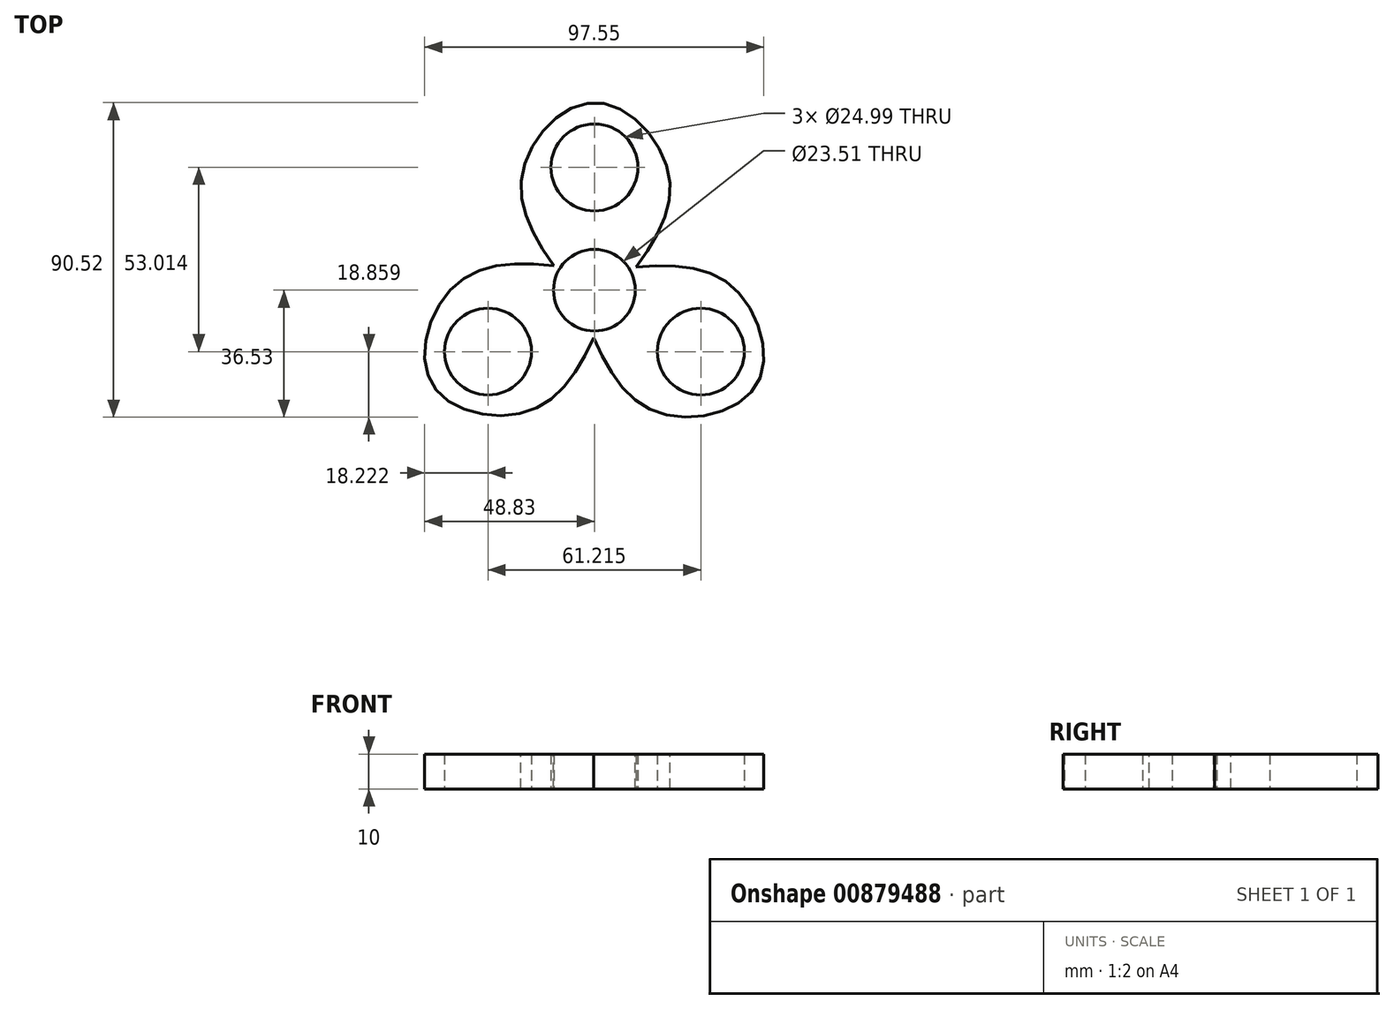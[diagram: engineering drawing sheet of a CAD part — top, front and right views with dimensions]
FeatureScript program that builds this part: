
annotation { "Feature Type Name" : "Feature", "Feature Type Description" : "" }
export const myFeature = defineFeature(function(context is Context, id is Id, definition is map)
    precondition{}
    {
        {
            var Q0;
            Q0=qCreatedBy(makeId("Top.planeOp"),FACE);
            var sketch = newSketch(context, id + "F0", { "sketchPlane" : qUnion([Q0])});
            skFitSpline(sketch, "E0", {"points": [v(-6.47, 0) * mm, v(-20.9, 32.64) * mm, v(0, 54) * mm, v(21.5, 32.64) * mm, v(7.07, 0) * mm], "startDerivative": vector(-92.56, 122.62) * mm, "endDerivative": vector(-93.29, -122.7) * mm});
            skLineSegment(sketch, "E1", {"start": v(-6.47, 0) * mm, "end": v(7.07, 0) * mm});
            skSolve(sketch);
        }
        {
            var Q0;
            Q0=makeQuery(id+"F0.imprint","IMPRINT",FACE,{"disambiguationData":[TD([[makeQuery(id+"F0.imprint","IMPRINT",EDGE,{"derivedFrom":sQuery(id+"F0.wireOp",EDGE,"E0")}),-1.0]])]});
            var sketch = newSketch(context, id + "F1", { "sketchPlane" : qUnion([Q0])});
            skCircle(sketch, "E2", {"center": v(0, 35.34) * mm, "radius": 12.5 * mm});
            skSolve(sketch);
        }
        {
            var Q0;
            Q0=makeQuery(id+"F0.imprint","IMPRINT",FACE,{"disambiguationData":[TD([[makeQuery(id+"F0.imprint","IMPRINT",EDGE,{"derivedFrom":sQuery(id+"F0.wireOp",EDGE,"E0")}),-1.0]])]});
            extrude(context, id + "F2", {"entities" : qUnion([Q0]), "depth" : 10 * mm, "offsetDistance" : 25.4 * mm});
        }
        {
            var Q0;
            Q0=makeQuery(id+"F1.imprint","IMPRINT",FACE,{"disambiguationData":[TD([[makeQuery(id+"F1.imprint","IMPRINT",EDGE,{"derivedFrom":sQuery(id+"F1.wireOp",EDGE,"E2")}),1.0]])]});
            extrude(context, id + "F3", {"entities" : qUnion([Q0]), "operationType" : NewBodyOperationType.REMOVE, "depth" : 10 * mm, "offsetDistance" : 25 * mm});
        }
        {
            var Q0;
            Q0=qCreatedBy(makeId("Front.planeOp"),FACE);
            var sketch = newSketch(context, id + "F4", { "sketchPlane" : qUnion([Q0])});
            skLineSegment(sketch, "E3", {"start": v(0, 0) * mm, "end": v(0, 27.4) * mm});
            skSolve(sketch);
        }
        {
            var Q0;
            Q0=makeQuery(id+"F2.opExtrude","SWEPT_BODY",BODY,{"disambiguationData":[OSD([sQuery(id+"F0.wireOp",EDGE,"E0"),sQuery(id+"F0.wireOp",EDGE,"E1")])]});
            var Q1;
            Q1=sQuery(id+"F4.wireOp",EDGE,"E3");
            circularPattern(context, id + "F5", {"entities" : qUnion([Q0]), "axis" : qUnion([Q1]), "angle" : 360 * degree, "instanceCount" : 3, "equalSpace" : true});
        }
        {
            var Q0;
            Q0=makeQuery(id+"F2.opExtrude","SWEPT_BODY",BODY,{"disambiguationData":[OSD([sQuery(id+"F0.wireOp",EDGE,"E0"),sQuery(id+"F0.wireOp",EDGE,"E1")])]});
            var Q1;
            Q1=makeQuery(id+"F5.opPattern","COPY",BODY,{"derivedFrom":makeQuery(id+"F2.opExtrude","SWEPT_BODY",BODY,{"disambiguationData":[OSD([sQuery(id+"F0.wireOp",EDGE,"E0"),sQuery(id+"F0.wireOp",EDGE,"E1")])]}),"instanceName":"2"});
            var Q2;
            Q2=makeQuery(id+"F5.opPattern","COPY",BODY,{"derivedFrom":makeQuery(id+"F2.opExtrude","SWEPT_BODY",BODY,{"disambiguationData":[OSD([sQuery(id+"F0.wireOp",EDGE,"E0"),sQuery(id+"F0.wireOp",EDGE,"E1")])]}),"instanceName":"1"});
            booleanBodies(context, id + "F6", {"operationType" : BooleanOperationType.UNION, "tools" : qUnion([Q0, Q1, Q2])});
        }
        {
            var Q0;
            {var subQ0=makeQuery(id+"F2.opExtrude","CAP_FACE",FACE,{"disambiguationData":[OSD([sQuery(id+"F0.wireOp",EDGE,"E0"),sQuery(id+"F0.wireOp",EDGE,"E1")])],"isStart":false});Q0=makeQuery(id+"F6.opBoolean","MERGE",FACE,{"derivedFrom":[subQ0,makeQuery(id+"F5.opPattern","COPY",FACE,{"derivedFrom":subQ0,"instanceName":"1"}),makeQuery(id+"F5.opPattern","COPY",FACE,{"derivedFrom":subQ0,"instanceName":"2"})]});}
            var sketch = newSketch(context, id + "F7", { "sketchPlane" : qUnion([Q0])});
            skCircle(sketch, "E4", {"center": v(0, 0) * mm, "radius": 11.76 * mm});
            skSolve(sketch);
        }
        {
            var Q0;
            Q0=makeQuery(id+"F7.imprint","IMPRINT",FACE,{"disambiguationData":[TD([[makeQuery(id+"F7.imprint","IMPRINT",EDGE,{"derivedFrom":sQuery(id+"F7.wireOp",EDGE,"E4")}),1.0]])]});
            extrude(context, id + "F8", {"entities" : qUnion([Q0]), "operationType" : NewBodyOperationType.REMOVE, "oppositeDirection" : true, "depth" : 25 * mm, "offsetDistance" : 25 * mm});
        }
    });
